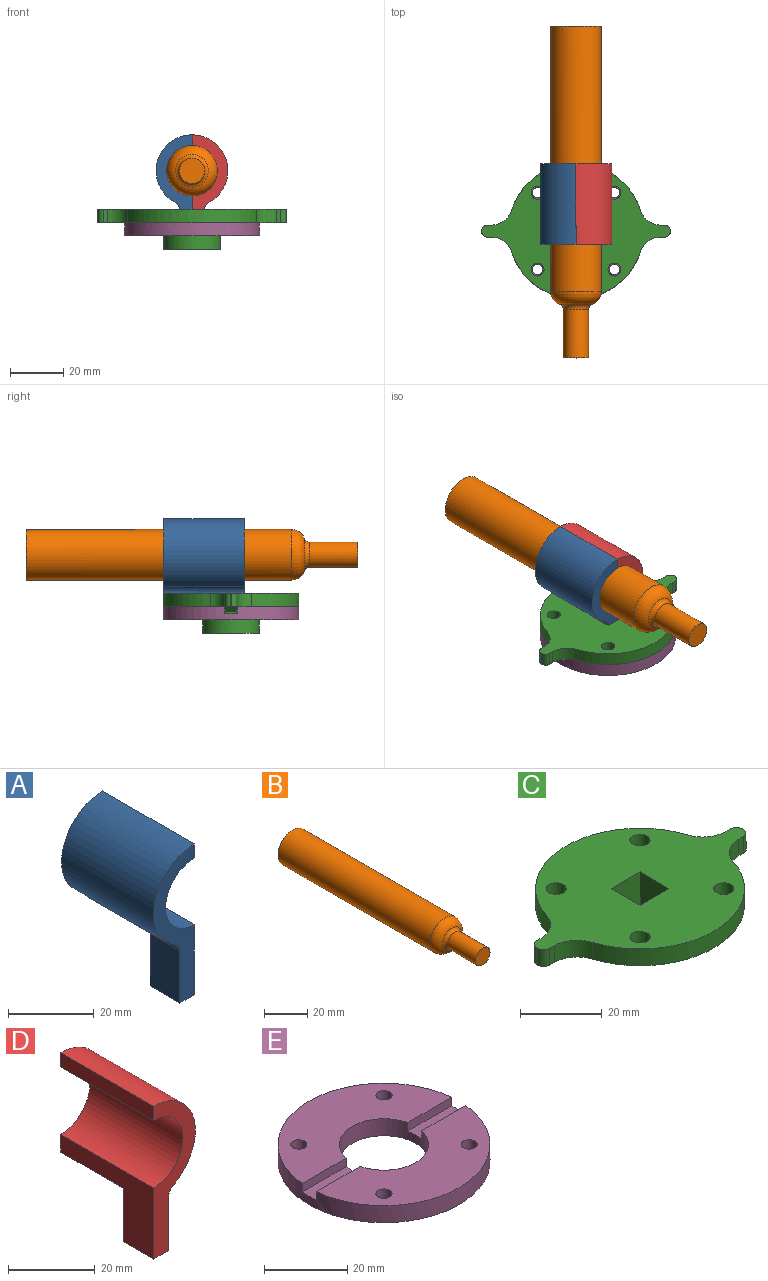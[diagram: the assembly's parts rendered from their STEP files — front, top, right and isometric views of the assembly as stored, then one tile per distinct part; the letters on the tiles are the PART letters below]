
ASSEMBLY  parts=5 mates=7
PART A: 11 faces, bbox 13.5x30.3x43.1 mm
  f0: plane 14.96x9.8mm, normal (-1,0,0), area 146.6mm2, adj f3,f5,f6,f10
  f1: plane 28.05x13.53mm, normal (0,1,0), area 151.6mm2, adj f2,f4,f7,f8,f9,f10
  f2: plane 30.3x20mm, normal (1,0,0), area 298.5mm2, adj f1,f3,f4,f5,f6,f7
  f3: plane 43.05x13.53mm, normal (0,-1,0), area 223.6mm2, adj f0,f2,f5,f7,f8,f9,f10
  f4: plane 20.5x4.8mm, normal (0,0,-1), area 98.4mm2, adj f1,f2,f6,f10
  f5: plane 9.8x4.8mm, normal (0,0,-1), area 47mm2, adj f0,f2,f3,f6
  f6: plane 15x4.8mm, normal (0,1,0), area 72mm2, adj f0,f2,f4,f5,f10
  f7: cylinder r=9.53mm len=30.3mm, axis (0,1,0), area 906.7mm2, adj f1,f2,f3,f8
  f8: plane 30.3x4mm, normal (1,0,0), area 121.2mm2, adj f1,f3,f7,f9
  f9: cylinder r=13.53mm len=30.3mm, axis (0,1,0), area 1086mm2, adj f1,f3,f8,f10
  f10: cylinder r=3mm len=30.3mm, axis (0,1,0), area 97.2mm2, adj f0,f1,f3,f4,f6,f9
PART B: 6 faces, bbox 19.1x125x19.1 mm
  f0: cylinder r=9.53mm len=100.01mm, axis (0,1,0), area 5985.1mm2, adj f1,f4
  f1: plane 19.05x19.05mm, normal (0,1,0), area 285mm2, adj f0
  f2: cylinder r=4.76mm len=18.36mm, axis (0,-1,0), area 549.4mm2, adj f3,f5
  f3: plane 9.53x9.53mm, normal (0,-1,0), area 71.3mm2, adj f2
  f4: torus R=4.53mm, axis (0,-1,0), area 325.9mm2, adj f0,f5
  f5: torus R=6.76mm, axis (0,-1,0), area 82mm2, adj f2,f4
PART C: 36 faces, bbox 71x51x15 mm
  f0: plane 71x51mm, normal (0,0,-1), area 1590.7mm2, adj f4,f5,f6,f7,f8,f9,f10,f11
  f1: plane 15x10mm, normal (1,0,0), area 150mm2, adj f2,f16,f17,f19
  f2: plane 15x10mm, normal (0,-1,0), area 150mm2, adj f1,f3,f17,f19
  f3: plane 15x10mm, normal (-1,0,0), area 150mm2, adj f2,f16,f17,f19
  f4: plane 5x1.61mm, normal (0,-1,0), area 8mm2, adj f0,f17,f27,f31
  f5: cylinder r=25.5mm len=48.55mm, axis (0,0,-1), area 321.3mm2, adj f0,f17,f27,f29
  f6: plane 5x1.61mm, normal (0,-1,0), area 8mm2, adj f0,f17,f29,f32
  f7: plane 5x0.5mm, normal (1,0,0), area 2.5mm2, adj f0,f17,f32,f33
  f8: plane 5x1.61mm, normal (0,1,0), area 8mm2, adj f0,f17,f28,f33
  f9: cylinder r=25.5mm len=48.55mm, axis (0,0,-1), area 321.3mm2, adj f0,f17,f26,f28
  f10: plane 5x1.61mm, normal (0,1,0), area 8mm2, adj f0,f17,f26,f30
  f11: cylinder r=2.45mm len=5mm, axis (0,0,-1), area 77mm2, adj f0,f17
  f12: cylinder r=2.45mm len=5mm, axis (0,0,-1), area 77mm2, adj f0,f17
  f13: cylinder r=2.45mm len=5mm, axis (0,0,-1), area 77mm2, adj f0,f17
  f14: cylinder r=2.45mm len=5mm, axis (0,0,-1), area 77mm2, adj f0,f17
  f15: plane 5x0.5mm, normal (-1,0,0), area 2.5mm2, adj f0,f17,f30,f31
  f16: plane 15x10mm, normal (0,1,0), area 150mm2, adj f1,f3,f17,f19
  f17: plane 71x51mm, normal (0,0,1), area 1984.6mm2, adj f1,f2,f3,f4,f5,f6,f7,f8
  f18: cylinder r=10.71mm len=21.42mm, axis (0,0,1), area 654.8mm2, adj f0,f19,f20,f21,f22,f23,f24,f25
  f19: plane 21.42x21.42mm, normal (0,0,-1), area 260.4mm2, adj f1,f2,f3,f16,f18
  f20: plane 14.93x2mm, normal (0,1,0), area 25.8mm2, adj f0,f18,f22,f34
  f21: plane 14.93x2mm, normal (0,-1,0), area 25.8mm2, adj f0,f18,f22,f34
  f22: plane 11.03x4.5mm, normal (0,0,-1), area 48.7mm2, adj f18,f20,f21,f34
  f23: plane 14.93x2mm, normal (0,1,0), area 25.8mm2, adj f0,f18,f25,f35
  f24: plane 14.93x2mm, normal (0,-1,0), area 25.8mm2, adj f0,f18,f25,f35
  f25: plane 11.03x4.5mm, normal (0,0,-1), area 48.7mm2, adj f18,f23,f24,f35
  f26: cylinder r=8mm len=7.62mm, axis (0,0,-1), area 50.4mm2, adj f0,f9,f10,f17
  f27: cylinder r=8mm len=7.62mm, axis (0,0,-1), area 50.4mm2, adj f0,f4,f5,f17
  f28: cylinder r=8mm len=7.62mm, axis (0,0,-1), area 50.4mm2, adj f0,f8,f9,f17
  f29: cylinder r=8mm len=7.62mm, axis (0,0,-1), area 50.4mm2, adj f0,f5,f6,f17
  f30: cylinder r=2mm len=5mm, axis (0,0,1), area 15.7mm2, adj f0,f10,f15,f17
  f31: cylinder r=2mm len=5mm, axis (0,0,-1), area 15.7mm2, adj f0,f4,f15,f17
  f32: cylinder r=2mm len=5mm, axis (0,0,1), area 15.7mm2, adj f0,f6,f7,f17
  f33: cylinder r=2mm len=5mm, axis (0,0,-1), area 15.7mm2, adj f0,f7,f8,f17
  f34: cone r=25.5mm half-angle=63.4deg, axis (0,0,1), area 20.2mm2, adj f0,f20,f21,f22
  f35: cone r=25.5mm half-angle=63.4deg, axis (0,0,1), area 20.2mm2, adj f0,f23,f24,f25
PART D: 11 faces, bbox 13.5x30.3x43.1 mm
  f0: plane 14.96x9.8mm, normal (1,0,0), area 146.6mm2, adj f3,f5,f6,f10
  f1: plane 28.05x13.53mm, normal (0,1,0), area 151.6mm2, adj f2,f4,f7,f8,f9,f10
  f2: plane 30.3x20mm, normal (-1,0,0), area 298.5mm2, adj f1,f3,f4,f5,f6,f7
  f3: plane 43.05x13.53mm, normal (0,-1,0), area 223.6mm2, adj f0,f2,f5,f7,f8,f9,f10
  f4: plane 20.5x4.8mm, normal (0,0,-1), area 98.4mm2, adj f1,f2,f6,f10
  f5: plane 9.8x4.8mm, normal (0,0,-1), area 47mm2, adj f0,f2,f3,f6
  f6: plane 15x4.8mm, normal (0,1,0), area 72mm2, adj f0,f2,f4,f5,f10
  f7: cylinder r=9.53mm len=30.3mm, axis (0,1,0), area 906.7mm2, adj f1,f2,f3,f8
  f8: plane 30.3x4mm, normal (-1,0,0), area 121.2mm2, adj f1,f3,f7,f9
  f9: cylinder r=13.53mm len=30.3mm, axis (0,1,0), area 1086mm2, adj f1,f3,f8,f10
  f10: cylinder r=3mm len=30.3mm, axis (0,1,0), area 97.2mm2, adj f0,f1,f3,f4,f6,f9
PART E: 15 faces, bbox 51x51x5 mm
  f0: cylinder r=10.71mm len=21.42mm, axis (0,0,-1), area 312.3mm2, adj f1,f2,f8,f9,f10,f11,f12,f13
  f1: plane 50.77x23.1mm, normal (0,0,1), area 746.1mm2, adj f0,f3,f6,f7,f9,f12
  f2: plane 50.77x23.1mm, normal (0,0,1), area 746.1mm2, adj f0,f4,f5,f7,f10,f13
  f3: cylinder r=1.95mm len=5mm, axis (0,0,-1), area 61.3mm2, adj f1,f8
  f4: cylinder r=1.95mm len=5mm, axis (0,0,-1), area 61.3mm2, adj f2,f8
  f5: cylinder r=1.95mm len=5mm, axis (0,0,-1), area 61.3mm2, adj f2,f8
  f6: cylinder r=1.95mm len=5mm, axis (0,0,-1), area 61.3mm2, adj f1,f8
  f7: cylinder r=25.5mm len=51mm, axis (0,0,-1), area 777.1mm2, adj f1,f2,f8,f9,f10,f11,f12,f13
  f8: plane 51x51mm, normal (0,0,-1), area 1634.7mm2, adj f0,f3,f4,f5,f6,f7
  f9: plane 14.95x2.5mm, normal (0,1,0), area 37.4mm2, adj f0,f1,f7,f11
  f10: plane 14.95x2.5mm, normal (0,-1,0), area 37.4mm2, adj f0,f2,f7,f11
  f11: plane 15.06x4.8mm, normal (0,0,1), area 71.2mm2, adj f0,f7,f9,f10
  f12: plane 14.95x2.5mm, normal (0,1,0), area 37.4mm2, adj f0,f1,f7,f14
  f13: plane 14.95x2.5mm, normal (0,-1,0), area 37.4mm2, adj f0,f2,f7,f14
  f14: plane 15.06x4.8mm, normal (0,0,1), area 71.2mm2, adj f0,f7,f12,f13
PLACE A t=(0,-0.2,0)mm
PLACE B rot(axis=(0,1,0),90deg) t=(0,14.69,24.53)mm
PLACE C at identity
PLACE D t=(0,-0.2,0)mm
PLACE E at identity
MATE planar C.f19 <-> A.f5  axis (0,0,-1) through (0,-5,-5)mm
MATE cylindrical D.f7 <-> B.f0  axis (0,1,0) through (0,25.3,24.53)mm
MATE slider B.f0 <-> A.f7  axis (0,1,0) through (0,77.19,24.53)mm
MATE planar C.f13 <-> E.f4  axis (0,0,-1) through (14.48,14.48,5)mm
MATE slider E.f0 <-> C.f5  axis (0,0,-1) through (0,0,0)mm
MATE slider A.f2 <-> D.f2  axis (1,0,0) through (0,4.8,10)mm
MATE slider C.f19 <-> D.f5  axis (0,0,-1) through (0,-5,-5)mm
